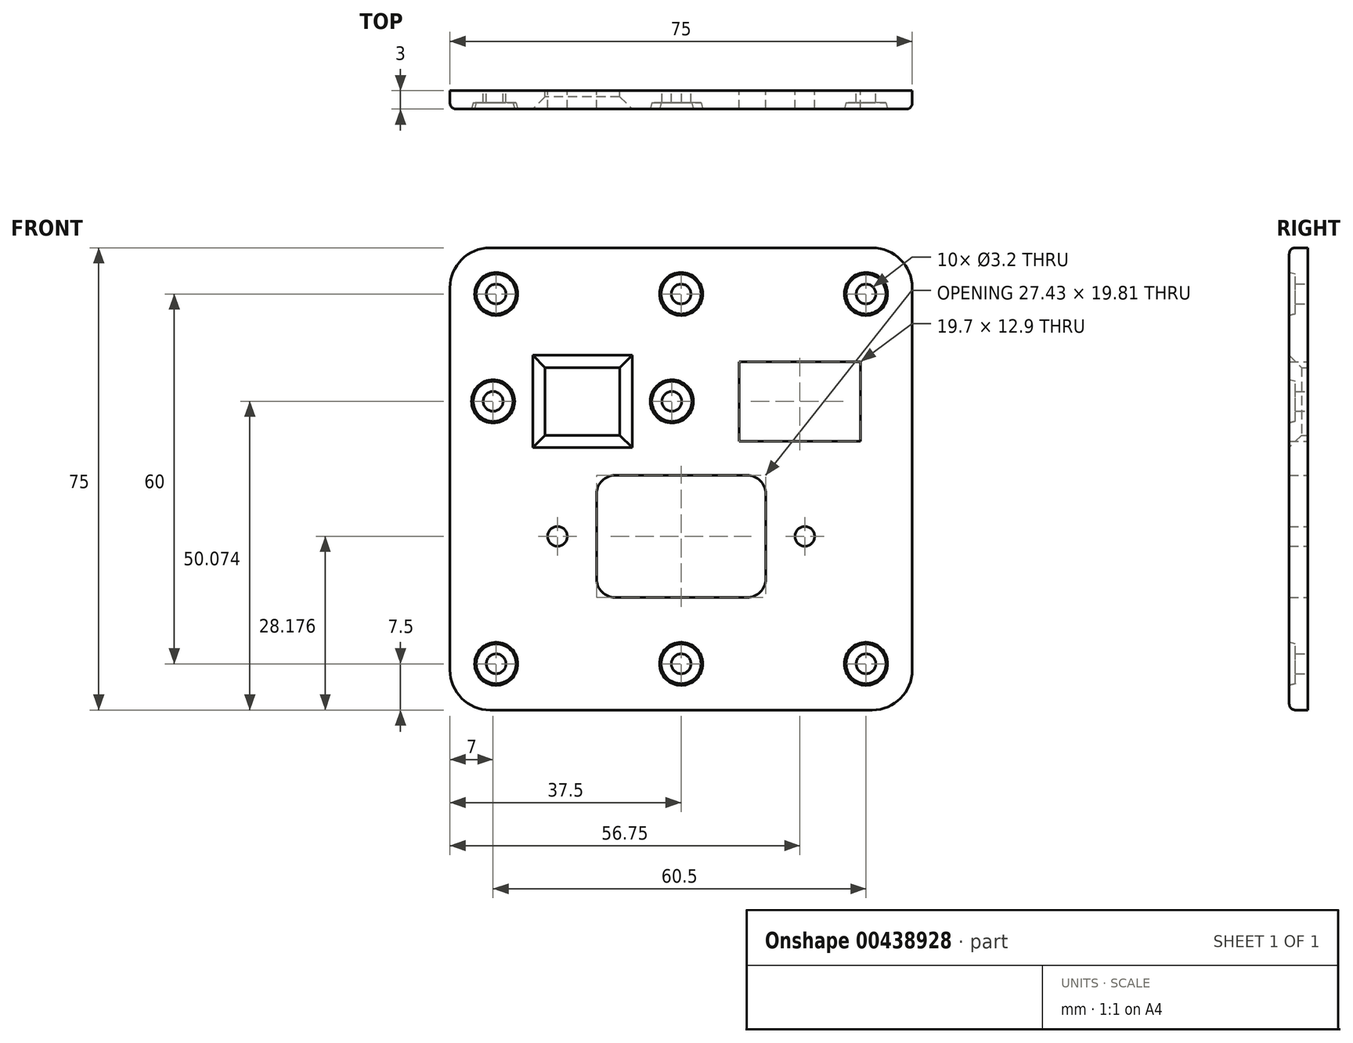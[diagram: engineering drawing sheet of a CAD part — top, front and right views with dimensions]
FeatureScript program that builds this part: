
annotation { "Feature Type Name" : "Feature", "Feature Type Description" : "" }
export const myFeature = defineFeature(function(context is Context, id is Id, definition is map)
    precondition{}
    {
        {
            var Q0;
            Q0=qCreatedBy(makeId("Front.planeOp"),FACE);
            var sketch = newSketch(context, id + "F0", { "sketchPlane" : qUnion([Q0])});
            skLineSegment(sketch, "E0.bottom", {"start": v(6.5, 75) * mm, "end": v(68.5, 75) * mm});
            skLineSegment(sketch, "E0.top", {"start": v(6.5, 0) * mm, "end": v(68.5, 0) * mm});
            skLineSegment(sketch, "E0.left", {"start": v(0, 68.5) * mm, "end": v(0, 6.5) * mm});
            skLineSegment(sketch, "E0.right", {"start": v(75, 68.5) * mm, "end": v(75, 6.5) * mm});
            skCircle(sketch, "E1", {"center": v(7.5, 67.5) * mm, "radius": 1.6 * mm});
            skCircle(sketch, "E2", {"center": v(37.5, 67.5) * mm, "radius": 1.6 * mm});
            skCircle(sketch, "E3", {"center": v(67.5, 67.5) * mm, "radius": 1.6 * mm});
            skCircle(sketch, "E4", {"center": v(7.5, 7.5) * mm, "radius": 1.6 * mm});
            skCircle(sketch, "E5", {"center": v(37.5, 7.5) * mm, "radius": 1.6 * mm});
            skCircle(sketch, "E6", {"center": v(67.5, 7.5) * mm, "radius": 1.6 * mm});
            skLineSegment(sketch, "E7", {"start": v(7.5, 67.5) * mm, "end": v(37.5, 67.5) * mm, "construction": true});
            skLineSegment(sketch, "E8", {"start": v(67.5, 67.5) * mm, "end": v(37.5, 67.5) * mm, "construction": true});
            skLineSegment(sketch, "E9.bottom", {"start": v(15.45, 55.57) * mm, "end": v(27.55, 55.57) * mm});
            skLineSegment(sketch, "E9.top", {"start": v(15.45, 44.57) * mm, "end": v(27.55, 44.57) * mm});
            skLineSegment(sketch, "E9.left", {"start": v(15.45, 55.57) * mm, "end": v(15.45, 44.57) * mm});
            skLineSegment(sketch, "E9.right", {"start": v(27.55, 55.57) * mm, "end": v(27.55, 44.57) * mm});
            skCircle(sketch, "E10", {"center": v(7, 50.07) * mm, "radius": 1.6 * mm});
            skCircle(sketch, "E11", {"center": v(36, 50.07) * mm, "radius": 1.6 * mm});
            skLineSegment(sketch, "E12", {"start": v(7, 50.07) * mm, "end": v(36, 50.07) * mm, "construction": true});
            skPoint(sketch, "E13.endSnap0", {"position": v(21.5, 50.07) * mm});
            skPoint(sketch, "E14.endSnap0", {"position": v(21.5, 44.57) * mm});
            skLineSegment(sketch, "E15", {"start": v(21.5, 55.57) * mm, "end": v(21.5, 50.07) * mm, "construction": true});
            skLineSegment(sketch, "E16", {"start": v(21.5, 44.57) * mm, "end": v(21.5, 50.07) * mm, "construction": true});
            skLineSegment(sketch, "E17", {"start": v(9.75, 50.07) * mm, "end": v(33.25, 50.07) * mm, "construction": true});
            skArc(sketch, "E18.0.startCap", {"start": v(9.75, 42.57) * mm, "mid": v(2.25, 50.07) * mm, "end": v(9.75, 57.57) * mm, "construction": true});
            skArc(sketch, "E18.0.endCap", {"start": v(33.25, 57.57) * mm, "mid": v(40.75, 50.07) * mm, "end": v(33.25, 42.57) * mm, "construction": true});
            skLineSegment(sketch, "E18.0.left", {"start": v(9.75, 57.57) * mm, "end": v(33.25, 57.57) * mm, "construction": true});
            skLineSegment(sketch, "E18.0.right", {"start": v(9.75, 42.57) * mm, "end": v(33.25, 42.57) * mm, "construction": true});
            skLineSegment(sketch, "E19.8", {"start": v(48.22, 38.08) * mm, "end": v(26.79, 38.08) * mm});
            skLineSegment(sketch, "E19.9", {"start": v(51.21, 21.27) * mm, "end": v(51.22, 35.08) * mm});
            skLineSegment(sketch, "E19.10", {"start": v(26.78, 18.27) * mm, "end": v(48.21, 18.27) * mm});
            skLineSegment(sketch, "E19.11", {"start": v(23.79, 35.08) * mm, "end": v(23.78, 21.27) * mm});
            skArc(sketch, "E19.12", {"start": v(23.78, 21.27) * mm, "mid": v(24.66, 19.15) * mm, "end": v(26.78, 18.27) * mm});
            skArc(sketch, "E19.13", {"start": v(26.79, 38.08) * mm, "mid": v(24.66, 37.2) * mm, "end": v(23.79, 35.08) * mm});
            skCircle(sketch, "E19.14", {"center": v(57.56, 28.18) * mm, "radius": 1.6 * mm});
            skCircle(sketch, "E19.15", {"center": v(17.44, 28.18) * mm, "radius": 1.6 * mm});
            skArc(sketch, "E19.16", {"start": v(48.21, 18.27) * mm, "mid": v(50.34, 19.15) * mm, "end": v(51.21, 21.27) * mm});
            skArc(sketch, "E19.17", {"start": v(51.22, 35.08) * mm, "mid": v(50.34, 37.2) * mm, "end": v(48.22, 38.08) * mm});
            skLineSegment(sketch, "E20", {"start": v(17.44, 28.18) * mm, "end": v(57.56, 28.18) * mm, "construction": true});
            skLineSegment(sketch, "E21", {"start": v(37.5, 28.18) * mm, "end": v(37.5, 18.27) * mm, "construction": true});
            skLineSegment(sketch, "E22", {"start": v(37.5, 28.18) * mm, "end": v(37.5, 38.08) * mm, "construction": true});
            skPoint(sketch, "E23.visualSharp", {"position": v(0, 75) * mm});
            skArc(sketch, "E23.filletArc", {"start": v(6.5, 75) * mm, "mid": v(1.9, 73.1) * mm, "end": v(0, 68.5) * mm});
            skPoint(sketch, "E24.visualSharp", {"position": v(75, 75) * mm});
            skArc(sketch, "E24.filletArc", {"start": v(75, 68.5) * mm, "mid": v(73.1, 73.1) * mm, "end": v(68.5, 75) * mm});
            skPoint(sketch, "E25.visualSharp", {"position": v(75, 0) * mm});
            skArc(sketch, "E25.filletArc", {"start": v(68.5, 0) * mm, "mid": v(73.1, 1.9) * mm, "end": v(75, 6.5) * mm});
            skPoint(sketch, "E26.visualSharp", {"position": v(0, 0) * mm});
            skArc(sketch, "E26.filletArc", {"start": v(0, 6.5) * mm, "mid": v(1.9, 1.9) * mm, "end": v(6.5, 0) * mm});
            skLineSegment(sketch, "E27.bottom", {"start": v(62.5, 39.43) * mm, "end": v(62.5, 16.93) * mm, "construction": true});
            skLineSegment(sketch, "E27.top", {"start": v(12.5, 39.43) * mm, "end": v(12.5, 16.93) * mm, "construction": true});
            skLineSegment(sketch, "E27.left", {"start": v(62.5, 39.43) * mm, "end": v(12.5, 39.43) * mm, "construction": true});
            skLineSegment(sketch, "E27.right", {"start": v(62.5, 16.93) * mm, "end": v(12.5, 16.93) * mm, "construction": true});
            skPoint(sketch, "E27.middle", {"position": v(37.5, 28.18) * mm});
            skLineSegment(sketch, "E28.bottom", {"start": v(66.6, 56.52) * mm, "end": v(46.9, 56.52) * mm});
            skLineSegment(sketch, "E28.top", {"start": v(66.6, 43.62) * mm, "end": v(46.9, 43.62) * mm});
            skLineSegment(sketch, "E28.left", {"start": v(66.6, 56.52) * mm, "end": v(66.6, 43.62) * mm});
            skLineSegment(sketch, "E28.right", {"start": v(46.9, 56.52) * mm, "end": v(46.9, 43.62) * mm});
            skPoint(sketch, "E28.middle", {"position": v(56.75, 50.07) * mm});
            skLineSegment(sketch, "E29.bottom", {"start": v(68, 57.57) * mm, "end": v(45.5, 57.57) * mm, "construction": true});
            skLineSegment(sketch, "E29.top", {"start": v(68, 42.57) * mm, "end": v(45.5, 42.57) * mm, "construction": true});
            skLineSegment(sketch, "E29.left", {"start": v(68, 57.57) * mm, "end": v(68, 42.57) * mm, "construction": true});
            skLineSegment(sketch, "E29.right", {"start": v(45.5, 57.57) * mm, "end": v(45.5, 42.57) * mm, "construction": true});
            skLineSegment(sketch, "E30", {"start": v(0, 60) * mm, "end": v(75, 60) * mm, "construction": true});
            skLineSegment(sketch, "E31", {"start": v(0, 15) * mm, "end": v(75, 15) * mm, "construction": true});
            skPoint(sketch, "E32", {"position": v(37.5, 75) * mm});
            skSolve(sketch);
        }
        {
            var Q0;
            Q0 = qSketchRegion(id + "F0", true);
            extrude(context, id + "F1", {"entities" : qUnion([Q0]), "depth" : 3 * mm});
        }
        {
            var Q0;
            Q0=makeQuery(id+"F1.opExtrude","CAP_FACE",FACE,{"disambiguationData":[OSD([sQuery(id+"F0.wireOp",EDGE,"E0.bottom"),sQuery(id+"F0.wireOp",EDGE,"E0.top"),sQuery(id+"F0.wireOp",EDGE,"E0.left"),sQuery(id+"F0.wireOp",EDGE,"E0.right"),sQuery(id+"F0.wireOp",EDGE,"E1"),sQuery(id+"F0.wireOp",EDGE,"E2"),sQuery(id+"F0.wireOp",EDGE,"E3"),sQuery(id+"F0.wireOp",EDGE,"E4"),sQuery(id+"F0.wireOp",EDGE,"E5"),sQuery(id+"F0.wireOp",EDGE,"E6"),sQuery(id+"F0.wireOp",EDGE,"E9.bottom"),sQuery(id+"F0.wireOp",EDGE,"E9.top"),sQuery(id+"F0.wireOp",EDGE,"E9.left"),sQuery(id+"F0.wireOp",EDGE,"E9.right"),sQuery(id+"F0.wireOp",EDGE,"E10"),sQuery(id+"F0.wireOp",EDGE,"E11"),sQuery(id+"F0.wireOp",EDGE,"E19.8"),sQuery(id+"F0.wireOp",EDGE,"E19.9"),sQuery(id+"F0.wireOp",EDGE,"E19.10"),sQuery(id+"F0.wireOp",EDGE,"E19.11"),sQuery(id+"F0.wireOp",EDGE,"E19.12"),sQuery(id+"F0.wireOp",EDGE,"E19.13"),sQuery(id+"F0.wireOp",EDGE,"E19.14"),sQuery(id+"F0.wireOp",EDGE,"E19.15"),sQuery(id+"F0.wireOp",EDGE,"E19.16"),sQuery(id+"F0.wireOp",EDGE,"E19.17"),sQuery(id+"F0.wireOp",EDGE,"E23.filletArc"),sQuery(id+"F0.wireOp",EDGE,"E24.filletArc"),sQuery(id+"F0.wireOp",EDGE,"E25.filletArc"),sQuery(id+"F0.wireOp",EDGE,"E26.filletArc"),sQuery(id+"F0.wireOp",EDGE,"E28.bottom"),sQuery(id+"F0.wireOp",EDGE,"E28.top"),sQuery(id+"F0.wireOp",EDGE,"E28.left"),sQuery(id+"F0.wireOp",EDGE,"E28.right")])],"isStart":false});
            var sketch = newSketch(context, id + "F2", { "sketchPlane" : qUnion([Q0])});
            skCircle(sketch, "E33", {"center": v(7.5, 67.5) * mm, "radius": 3.5 * mm});
            skCircle(sketch, "E34", {"center": v(37.5, 67.5) * mm, "radius": 3.5 * mm});
            skCircle(sketch, "E35", {"center": v(67.5, 67.5) * mm, "radius": 3.5 * mm});
            skCircle(sketch, "E36", {"center": v(36, 50.07) * mm, "radius": 3.5 * mm});
            skCircle(sketch, "E37", {"center": v(7, 50.07) * mm, "radius": 3.5 * mm});
            skCircle(sketch, "E38", {"center": v(67.5, 7.5) * mm, "radius": 3.5 * mm});
            skCircle(sketch, "E39", {"center": v(37.5, 7.5) * mm, "radius": 3.5 * mm});
            skCircle(sketch, "E40", {"center": v(7.5, 7.5) * mm, "radius": 3.5 * mm});
            skSolve(sketch);
        }
        {
            var Q0;
            Q0 = qSketchRegion(id + "F2", true);
            extrude(context, id + "F3", {"entities" : qUnion([Q0]), "operationType" : NewBodyOperationType.REMOVE, "oppositeDirection" : true, "depth" : 1 * mm, "hasDraft" : true, "draftAngle" : 15 * degree, "draftPullDirection" : true});
        }
        {
            var Q0;
            Q0=makeQuery(id+"F1.opExtrude","CAP_EDGE",EDGE,{"disambiguationData":[OSD([sQuery(id+"F0.wireOp",EDGE,"E0.top")])],"isStart":false});
            fillet(context, id + "F4", {"entities" : qUnion([Q0]), "radius" : 1 * mm, "tangentPropagation" : true, "allowEdgeOverflow" : false});
        }
        {
            var Q0;
            Q0=makeQuery(id+"F1.opExtrude","CAP_EDGE",EDGE,{"disambiguationData":[OSD([sQuery(id+"F0.wireOp",EDGE,"E9.bottom")])],"isStart":false});
            var Q1;
            Q1=makeQuery(id+"F1.opExtrude","CAP_EDGE",EDGE,{"disambiguationData":[OSD([sQuery(id+"F0.wireOp",EDGE,"E9.right")])],"isStart":false});
            var Q2;
            Q2=makeQuery(id+"F1.opExtrude","CAP_EDGE",EDGE,{"disambiguationData":[OSD([sQuery(id+"F0.wireOp",EDGE,"E9.top")])],"isStart":false});
            var Q3;
            Q3=makeQuery(id+"F1.opExtrude","CAP_EDGE",EDGE,{"disambiguationData":[OSD([sQuery(id+"F0.wireOp",EDGE,"E9.left")])],"isStart":false});
            chamfer(context, id + "F5", {"entities" : qUnion([Q0, Q1, Q2, Q3]), "width" : 2 * mm, "tangentPropagation" : true});
        }
    });
